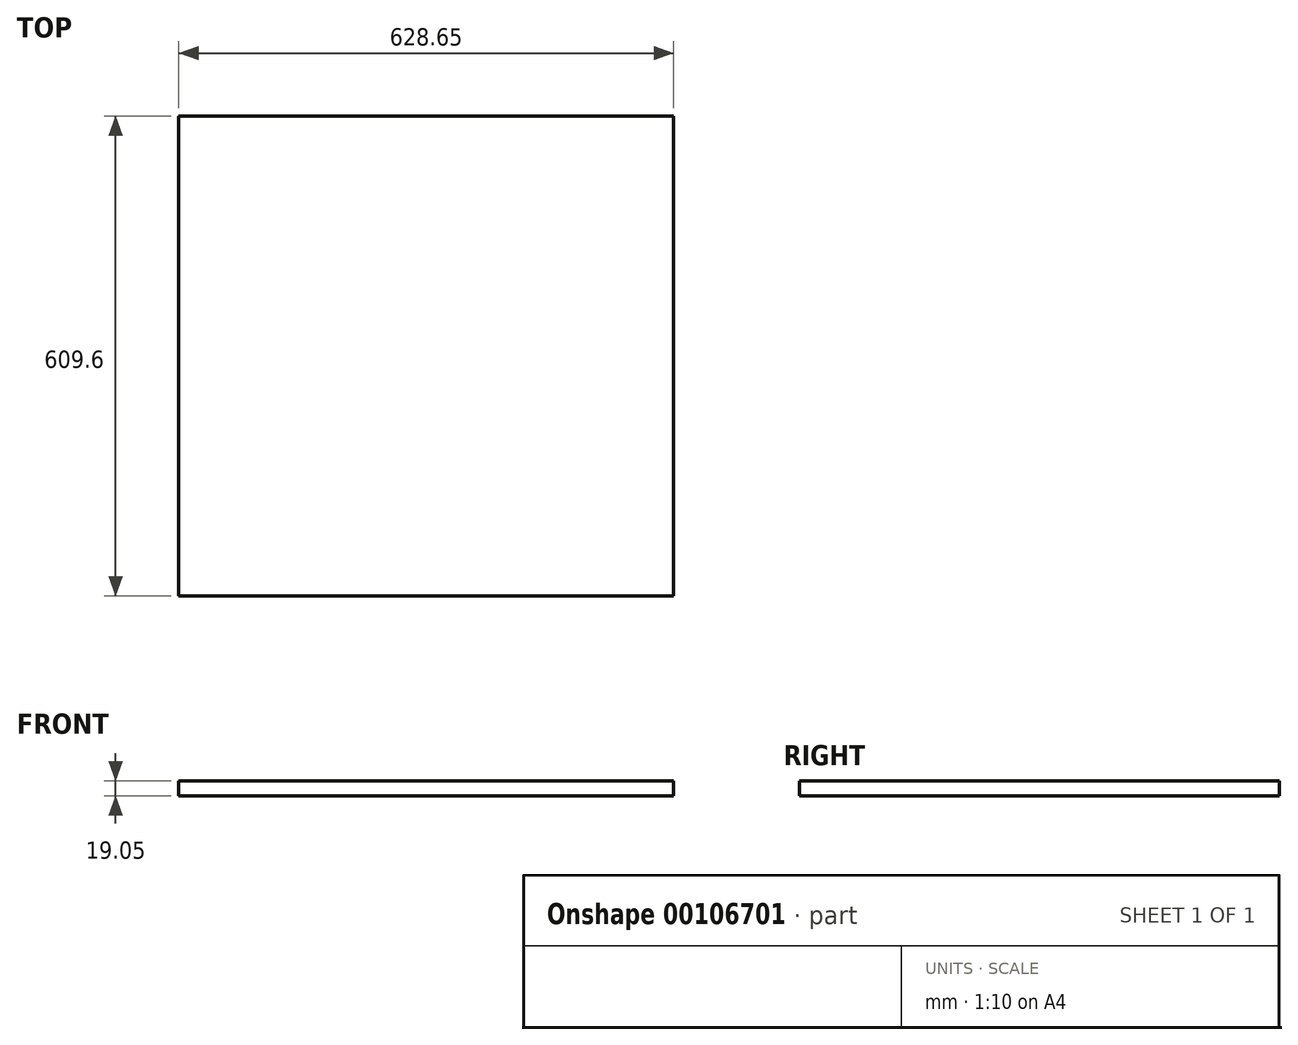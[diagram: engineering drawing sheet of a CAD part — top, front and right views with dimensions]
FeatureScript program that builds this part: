
annotation { "Feature Type Name" : "Feature", "Feature Type Description" : "" }
export const myFeature = defineFeature(function(context is Context, id is Id, definition is map)
    precondition{}
    {
        {
            var Q0;
            Q0=qCreatedBy(makeId("Top.planeOp"),FACE);
            var sketch = newSketch(context, id + "F0", { "sketchPlane" : qUnion([Q0])});
            skLineSegment(sketch, "E0.bottom", {"start": v(0, 0) * mm, "end": v(628.65, 0) * mm});
            skLineSegment(sketch, "E0.top", {"start": v(0, 609.6) * mm, "end": v(628.65, 609.6) * mm});
            skLineSegment(sketch, "E0.left", {"start": v(0, 0) * mm, "end": v(0, 609.6) * mm});
            skLineSegment(sketch, "E0.right", {"start": v(628.65, 0) * mm, "end": v(628.65, 609.6) * mm});
            skSolve(sketch);
        }
        {
            var Q0;
            Q0=makeQuery(id+"F0.imprint","IMPRINT",FACE,{"disambiguationData":[TD([[makeQuery(id+"F0.imprint","IMPRINT",EDGE,{"derivedFrom":sQuery(id+"F0.wireOp",EDGE,"E0.bottom")}),1.0]])]});
            extrude(context, id + "F1", {"entities" : qUnion([Q0]), "depth" : 19.05 * mm});
        }
    });
